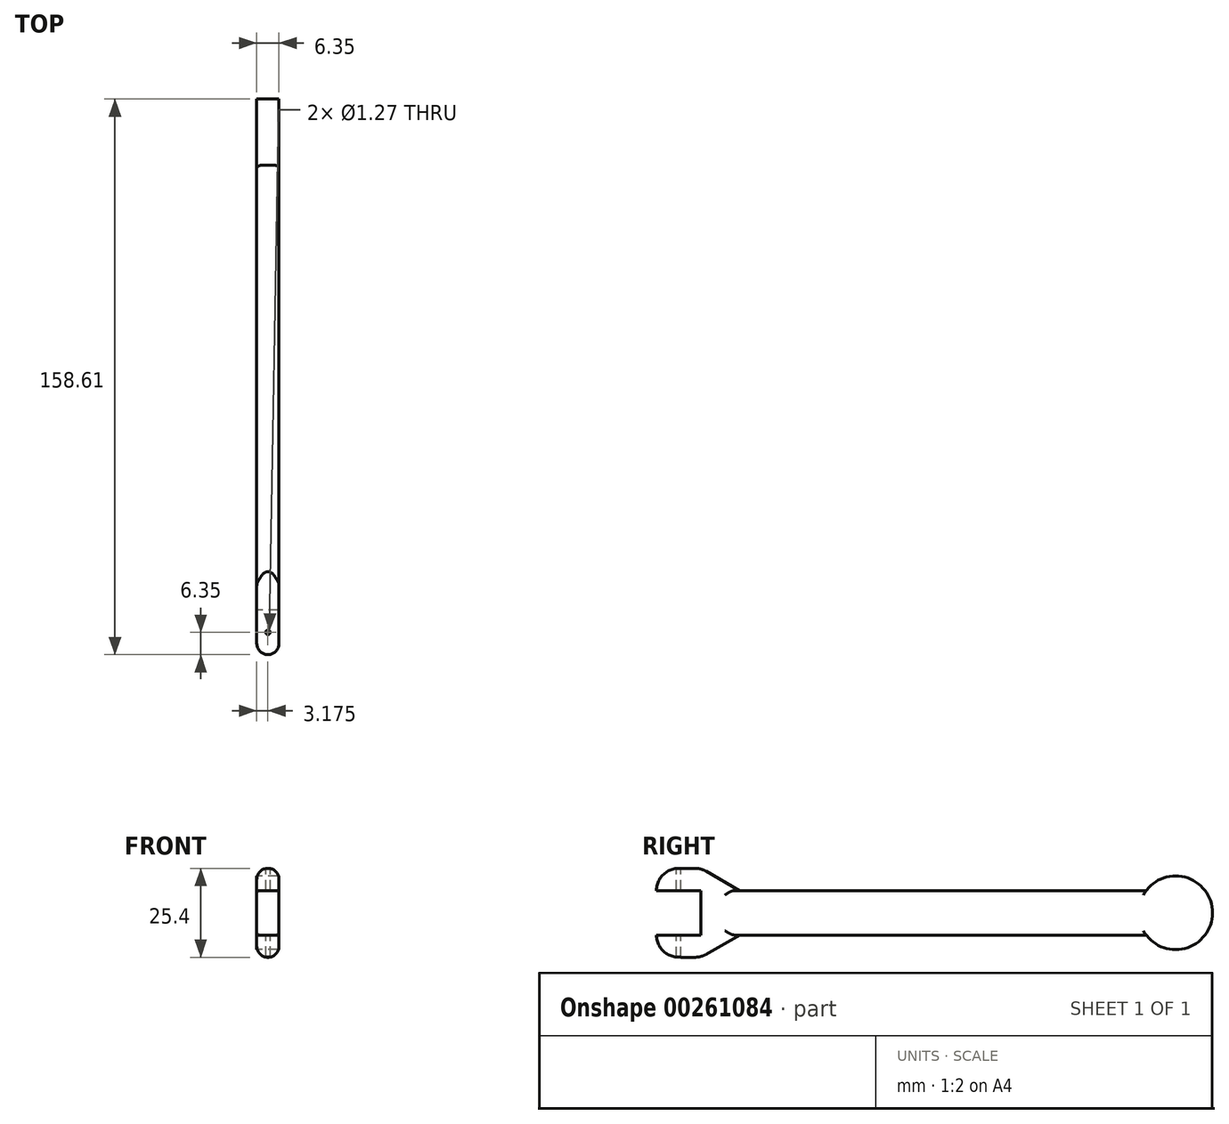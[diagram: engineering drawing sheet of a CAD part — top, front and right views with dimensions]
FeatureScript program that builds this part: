
annotation { "Feature Type Name" : "Feature", "Feature Type Description" : "" }
export const myFeature = defineFeature(function(context is Context, id is Id, definition is map)
    precondition{}
    {
        {
            var Q0;
            Q0=qCreatedBy(makeId("Right.planeOp"),FACE);
            var sketch = newSketch(context, id + "F0", { "sketchPlane" : qUnion([Q0])});
            skLineSegment(sketch, "E0.bottom", {"start": v(63.5, -6.35) * mm, "end": v(-63.5, -6.35) * mm});
            skLineSegment(sketch, "E0.top", {"start": v(63.5, 6.35) * mm, "end": v(-63.5, 6.35) * mm});
            skLineSegment(sketch, "E0.left", {"start": v(63.5, -6.35) * mm, "end": v(63.5, 6.35) * mm});
            skLineSegment(sketch, "E0.right", {"start": v(-63.5, -6.35) * mm, "end": v(-63.5, 6.35) * mm});
            skPoint(sketch, "E0.middle", {"position": v(0, 0) * mm});
            skCircle(sketch, "E1", {"center": v(71.89, 0) * mm, "radius": 10.52 * mm});
            skPoint(sketch, "E1.third.point", {"position": v(82.4, 0) * mm});
            skPoint(sketch, "E1.third.point.positionSnap0", {"position": v(63.5, 0) * mm});
            skLineSegment(sketch, "E2", {"start": v(-63.5, 6.35) * mm, "end": v(-63.5, 12.7) * mm});
            skLineSegment(sketch, "E3.bottom", {"start": v(-63.5, 12.7) * mm, "end": v(-76.2, 12.7) * mm});
            skLineSegment(sketch, "E3.top", {"start": v(-63.5, -12.7) * mm, "end": v(-76.2, -12.7) * mm});
            skLineSegment(sketch, "E3.left", {"start": v(-63.5, 12.7) * mm, "end": v(-63.5, -12.7) * mm});
            skLineSegment(sketch, "E3.right", {"start": v(-76.2, 12.7) * mm, "end": v(-76.2, -12.7) * mm});
            skLineSegment(sketch, "E4.bottom", {"start": v(-63.5, 6.35) * mm, "end": v(-76.2, 6.35) * mm});
            skLineSegment(sketch, "E4.top", {"start": v(-63.5, -6.35) * mm, "end": v(-76.2, -6.35) * mm});
            skLineSegment(sketch, "E4.left", {"start": v(-63.5, 6.35) * mm, "end": v(-63.5, -6.35) * mm});
            skLineSegment(sketch, "E4.right", {"start": v(-76.2, 6.35) * mm, "end": v(-76.2, -6.35) * mm});
            skLineSegment(sketch, "E5", {"start": v(-63.5, 12.7) * mm, "end": v(-52.5, 6.35) * mm});
            skLineSegment(sketch, "E6", {"start": v(-52.5, 6.35) * mm, "end": v(-63.5, 6.35) * mm});
            skLineSegment(sketch, "E7", {"start": v(-63.5, -12.7) * mm, "end": v(-52.5, -6.35) * mm});
            skLineSegment(sketch, "E8", {"start": v(-52.5, -6.35) * mm, "end": v(-63.5, -6.35) * mm});
            skSolve(sketch);
        }
        {
            var Q0;
            {var subQ0=sQuery(id+"F0.wireOp",EDGE,"E0.left");Q0=makeQuery(id+"F0.imprint","IMPRINT",FACE,{"disambiguationData":[TD([[makeQuery(id+"F0.imprint","IMPRINT",EDGE,{"derivedFrom":subQ0}),1.0]])]});}
            var Q1;
            {var subQ0=sQuery(id+"F0.wireOp",EDGE,"E0.left");Q1=makeQuery(id+"F0.imprint","IMPRINT",FACE,{"disambiguationData":[TD([[makeQuery(id+"F0.imprint","IMPRINT",EDGE,{"derivedFrom":subQ0}),-1.0]])]});}
            var Q2;
            {var subQ0=sQuery(id+"F0.wireOp",EDGE,"E0.bottom");Q2=makeQuery(id+"F0.imprint","IMPRINT",FACE,{"disambiguationData":[TD([[makeQuery(id+"F0.imprint","IMPRINT",EDGE,{"derivedFrom":subQ0}),-1.0]])]});}
            var Q3;
            {var subQ0=sQuery(id+"F0.wireOp",EDGE,"E3.bottom");Q3=makeQuery(id+"F0.imprint","IMPRINT",FACE,{"disambiguationData":[TD([[makeQuery(id+"F0.imprint","IMPRINT",EDGE,{"derivedFrom":subQ0}),1.0]])]});}
            var Q4;
            {var subQ0=sQuery(id+"F0.wireOp",EDGE,"E5");Q4=makeQuery(id+"F0.imprint","IMPRINT",FACE,{"disambiguationData":[TD([[makeQuery(id+"F0.imprint","IMPRINT",EDGE,{"derivedFrom":subQ0}),-1.0]])]});}
            var Q5;
            {var subQ0=sQuery(id+"F0.wireOp",EDGE,"E7");Q5=makeQuery(id+"F0.imprint","IMPRINT",FACE,{"disambiguationData":[TD([[makeQuery(id+"F0.imprint","IMPRINT",EDGE,{"derivedFrom":subQ0}),1.0]])]});}
            var Q6;
            {var subQ0=sQuery(id+"F0.wireOp",EDGE,"E3.top");Q6=makeQuery(id+"F0.imprint","IMPRINT",FACE,{"disambiguationData":[TD([[makeQuery(id+"F0.imprint","IMPRINT",EDGE,{"derivedFrom":subQ0}),-1.0]])]});}
            extrude(context, id + "F1", {"entities" : qUnion([Q0, Q1, Q2, Q3, Q4, Q5, Q6]), "depth" : 6.35 * mm});
        }
        {
            var Q0;
            Q0=makeQuery(id+"F1.opExtrude","SWEPT_EDGE",EDGE,{"disambiguationData":[OSD([sQuery(id+"F0.wireOp",EDGE,"E3.bottom"),sQuery(id+"F0.wireOp",EDGE,"E3.right")])]});
            var Q1;
            Q1=makeQuery(id+"F1.opExtrude","SWEPT_EDGE",EDGE,{"disambiguationData":[OSD([sQuery(id+"F0.wireOp",EDGE,"E3.top"),sQuery(id+"F0.wireOp",EDGE,"E3.right")])]});
            fillet(context, id + "F2", {"entities" : qUnion([Q0, Q1]), "radius" : 6.35 * mm, "tangentPropagation" : true, "allowEdgeOverflow" : false});
        }
        {
            var Q0;
            Q0=makeQuery(id+"F1.opExtrude","SWEPT_EDGE",EDGE,{"disambiguationData":[OSD([sQuery(id+"F0.wireOp",EDGE,"E3.bottom"),sQuery(id+"F0.wireOp",EDGE,"E3.left"),sQuery(id+"F0.wireOp",EDGE,"E5")])]});
            var Q1;
            Q1=makeQuery(id+"F1.opExtrude","SWEPT_EDGE",EDGE,{"disambiguationData":[OSD([sQuery(id+"F0.wireOp",EDGE,"E3.top"),sQuery(id+"F0.wireOp",EDGE,"E3.left"),sQuery(id+"F0.wireOp",EDGE,"E7")])]});
            fillet(context, id + "F3", {"entities" : qUnion([Q0, Q1]), "radius" : 6.35 * mm, "tangentPropagation" : true, "allowEdgeOverflow" : false});
        }
        {
            var Q0;
            Q0=makeQuery(id+"F1.opExtrude","SWEPT_FACE",FACE,{"disambiguationData":[OSD([sQuery(id+"F0.wireOp",EDGE,"E3.bottom")])]});
            var sketch = newSketch(context, id + "F4", { "sketchPlane" : qUnion([Q0])});
            skCircle(sketch, "E9", {"center": v(3.18, -69.85) * mm, "radius": 0.64 * mm});
            skSolve(sketch);
        }
        {
            var Q0;
            {var subQ0=sQuery(id+"F4.wireOp",EDGE,"E9");var subQ1=sQuery(id+"F0.wireOp",EDGE,"E3.bottom");var subQ2=makeQuery(id+"F2.opFillet","BLEND_EDGE",EDGE,{"blendedFrom":[makeQuery(id+"F1.opExtrude","SWEPT_EDGE",EDGE,{"disambiguationData":[OSD([subQ1,sQuery(id+"F0.wireOp",EDGE,"E3.right")])]}),makeQuery(id+"F1.opExtrude","SWEPT_FACE",FACE,{"disambiguationData":[OSD([subQ1])]})],"blendedInto":[makeQuery(id+"F1.opExtrude","SWEPT_FACE",FACE,{"disambiguationData":[OSD([subQ1])]})]});var subQ3=makeQuery(id+"F4.imprint","INTERSECT",VERTEX,{"disambiguationData":[OD(0.0)],"derivedFrom":[subQ2,subQ0]});Q0=makeQuery(id+"F4.imprint","IMPRINT",FACE,{"disambiguationData":[TD([[makeQuery(id+"F4.imprint","IMPRINT",EDGE,{"disambiguationData":[TD([[subQ3,1.0]])],"derivedFrom":subQ0}),1.0]])]});}
            var Q1;
            {var subQ0=sQuery(id+"F4.wireOp",EDGE,"E9");var subQ1=sQuery(id+"F0.wireOp",EDGE,"E3.bottom");var subQ2=makeQuery(id+"F2.opFillet","BLEND_EDGE",EDGE,{"blendedFrom":[makeQuery(id+"F1.opExtrude","SWEPT_EDGE",EDGE,{"disambiguationData":[OSD([subQ1,sQuery(id+"F0.wireOp",EDGE,"E3.right")])]}),makeQuery(id+"F1.opExtrude","SWEPT_FACE",FACE,{"disambiguationData":[OSD([subQ1])]})],"blendedInto":[makeQuery(id+"F1.opExtrude","SWEPT_FACE",FACE,{"disambiguationData":[OSD([subQ1])]})]});var subQ3=makeQuery(id+"F4.imprint","INTERSECT",VERTEX,{"disambiguationData":[OD(0.0)],"derivedFrom":[subQ2,subQ0]});Q1=makeQuery(id+"F4.imprint","IMPRINT",FACE,{"disambiguationData":[TD([[makeQuery(id+"F4.imprint","IMPRINT",EDGE,{"disambiguationData":[TD([[subQ3,-1.0]])],"derivedFrom":subQ0}),1.0]])]});}
            extrude(context, id + "F5", {"entities" : qUnion([Q0, Q1]), "operationType" : NewBodyOperationType.REMOVE, "oppositeDirection" : true, "depth" : 25.4 * mm});
        }
        {
            var Q0;
            Q0=makeQuery(id+"F1.opExtrude","CAP_EDGE",EDGE,{"disambiguationData":[OSD([sQuery(id+"F0.wireOp",EDGE,"E0.bottom")])],"isStart":false});
            var Q1;
            Q1=makeQuery(id+"F1.opExtrude","CAP_EDGE",EDGE,{"disambiguationData":[OSD([sQuery(id+"F0.wireOp",EDGE,"E0.bottom")])],"isStart":true});
            var Q2;
            Q2=makeQuery(id+"F1.opExtrude","CAP_EDGE",EDGE,{"disambiguationData":[OSD([sQuery(id+"F0.wireOp",EDGE,"E0.top")])],"isStart":false});
            var Q3;
            Q3=makeQuery(id+"F1.opExtrude","CAP_EDGE",EDGE,{"disambiguationData":[OSD([sQuery(id+"F0.wireOp",EDGE,"E0.top")])],"isStart":true});
            fillet(context, id + "F6", {"entities" : qUnion([Q0, Q1, Q2, Q3]), "radius" : 1.27 * mm, "tangentPropagation" : true, "allowEdgeOverflow" : false});
        }
        {
            var Q0;
            {var subQ0=sQuery(id+"F0.wireOp",EDGE,"E3.right");var subQ1=sQuery(id+"F0.wireOp",EDGE,"E3.bottom");Q0=makeQuery(id+"F2.opFillet","BLEND_EDGE",EDGE,{"blendedFrom":[makeQuery(id+"F1.opExtrude","SWEPT_EDGE",EDGE,{"disambiguationData":[OSD([subQ1,subQ0])]}),makeQuery(id+"F1.opExtrude","CAP_FACE",FACE,{"disambiguationData":[OSD([sQuery(id+"F0.wireOp",EDGE,"E0.bottom"),sQuery(id+"F0.wireOp",EDGE,"E0.top"),sQuery(id+"F0.wireOp",EDGE,"E1"),subQ1,sQuery(id+"F0.wireOp",EDGE,"E3.top"),subQ0,sQuery(id+"F0.wireOp",EDGE,"E4.bottom"),sQuery(id+"F0.wireOp",EDGE,"E4.top"),sQuery(id+"F0.wireOp",EDGE,"E4.left"),sQuery(id+"F0.wireOp",EDGE,"E5"),sQuery(id+"F0.wireOp",EDGE,"E7")])],"isStart":true})],"blendedInto":[makeQuery(id+"F1.opExtrude","CAP_FACE",FACE,{"disambiguationData":[OSD([sQuery(id+"F0.wireOp",EDGE,"E0.bottom"),sQuery(id+"F0.wireOp",EDGE,"E0.top"),sQuery(id+"F0.wireOp",EDGE,"E1"),subQ1,sQuery(id+"F0.wireOp",EDGE,"E3.top"),subQ0,sQuery(id+"F0.wireOp",EDGE,"E4.bottom"),sQuery(id+"F0.wireOp",EDGE,"E4.top"),sQuery(id+"F0.wireOp",EDGE,"E4.left"),sQuery(id+"F0.wireOp",EDGE,"E5"),sQuery(id+"F0.wireOp",EDGE,"E7")])],"isStart":true})]});}
            var Q1;
            {var subQ0=sQuery(id+"F0.wireOp",EDGE,"E3.right");var subQ1=sQuery(id+"F0.wireOp",EDGE,"E3.bottom");Q1=makeQuery(id+"F2.opFillet","BLEND_EDGE",EDGE,{"blendedFrom":[makeQuery(id+"F1.opExtrude","SWEPT_EDGE",EDGE,{"disambiguationData":[OSD([subQ1,subQ0])]}),makeQuery(id+"F1.opExtrude","CAP_FACE",FACE,{"disambiguationData":[OSD([sQuery(id+"F0.wireOp",EDGE,"E0.bottom"),sQuery(id+"F0.wireOp",EDGE,"E0.top"),sQuery(id+"F0.wireOp",EDGE,"E1"),subQ1,sQuery(id+"F0.wireOp",EDGE,"E3.top"),subQ0,sQuery(id+"F0.wireOp",EDGE,"E4.bottom"),sQuery(id+"F0.wireOp",EDGE,"E4.top"),sQuery(id+"F0.wireOp",EDGE,"E4.left"),sQuery(id+"F0.wireOp",EDGE,"E5"),sQuery(id+"F0.wireOp",EDGE,"E7")])],"isStart":false})],"blendedInto":[makeQuery(id+"F1.opExtrude","CAP_FACE",FACE,{"disambiguationData":[OSD([sQuery(id+"F0.wireOp",EDGE,"E0.bottom"),sQuery(id+"F0.wireOp",EDGE,"E0.top"),sQuery(id+"F0.wireOp",EDGE,"E1"),subQ1,sQuery(id+"F0.wireOp",EDGE,"E3.top"),subQ0,sQuery(id+"F0.wireOp",EDGE,"E4.bottom"),sQuery(id+"F0.wireOp",EDGE,"E4.top"),sQuery(id+"F0.wireOp",EDGE,"E4.left"),sQuery(id+"F0.wireOp",EDGE,"E5"),sQuery(id+"F0.wireOp",EDGE,"E7")])],"isStart":false})]});}
            var Q2;
            {var subQ0=sQuery(id+"F0.wireOp",EDGE,"E3.right");var subQ1=sQuery(id+"F0.wireOp",EDGE,"E3.top");Q2=makeQuery(id+"F2.opFillet","BLEND_EDGE",EDGE,{"blendedFrom":[makeQuery(id+"F1.opExtrude","SWEPT_EDGE",EDGE,{"disambiguationData":[OSD([subQ1,subQ0])]}),makeQuery(id+"F1.opExtrude","CAP_FACE",FACE,{"disambiguationData":[OSD([sQuery(id+"F0.wireOp",EDGE,"E0.bottom"),sQuery(id+"F0.wireOp",EDGE,"E0.top"),sQuery(id+"F0.wireOp",EDGE,"E1"),sQuery(id+"F0.wireOp",EDGE,"E3.bottom"),subQ1,subQ0,sQuery(id+"F0.wireOp",EDGE,"E4.bottom"),sQuery(id+"F0.wireOp",EDGE,"E4.top"),sQuery(id+"F0.wireOp",EDGE,"E4.left"),sQuery(id+"F0.wireOp",EDGE,"E5"),sQuery(id+"F0.wireOp",EDGE,"E7")])],"isStart":true})],"blendedInto":[makeQuery(id+"F1.opExtrude","CAP_FACE",FACE,{"disambiguationData":[OSD([sQuery(id+"F0.wireOp",EDGE,"E0.bottom"),sQuery(id+"F0.wireOp",EDGE,"E0.top"),sQuery(id+"F0.wireOp",EDGE,"E1"),sQuery(id+"F0.wireOp",EDGE,"E3.bottom"),subQ1,subQ0,sQuery(id+"F0.wireOp",EDGE,"E4.bottom"),sQuery(id+"F0.wireOp",EDGE,"E4.top"),sQuery(id+"F0.wireOp",EDGE,"E4.left"),sQuery(id+"F0.wireOp",EDGE,"E5"),sQuery(id+"F0.wireOp",EDGE,"E7")])],"isStart":true})]});}
            var Q3;
            {var subQ0=sQuery(id+"F0.wireOp",EDGE,"E3.right");var subQ1=sQuery(id+"F0.wireOp",EDGE,"E3.top");Q3=makeQuery(id+"F2.opFillet","BLEND_EDGE",EDGE,{"blendedFrom":[makeQuery(id+"F1.opExtrude","SWEPT_EDGE",EDGE,{"disambiguationData":[OSD([subQ1,subQ0])]}),makeQuery(id+"F1.opExtrude","CAP_FACE",FACE,{"disambiguationData":[OSD([sQuery(id+"F0.wireOp",EDGE,"E0.bottom"),sQuery(id+"F0.wireOp",EDGE,"E0.top"),sQuery(id+"F0.wireOp",EDGE,"E1"),sQuery(id+"F0.wireOp",EDGE,"E3.bottom"),subQ1,subQ0,sQuery(id+"F0.wireOp",EDGE,"E4.bottom"),sQuery(id+"F0.wireOp",EDGE,"E4.top"),sQuery(id+"F0.wireOp",EDGE,"E4.left"),sQuery(id+"F0.wireOp",EDGE,"E5"),sQuery(id+"F0.wireOp",EDGE,"E7")])],"isStart":false})],"blendedInto":[makeQuery(id+"F1.opExtrude","CAP_FACE",FACE,{"disambiguationData":[OSD([sQuery(id+"F0.wireOp",EDGE,"E0.bottom"),sQuery(id+"F0.wireOp",EDGE,"E0.top"),sQuery(id+"F0.wireOp",EDGE,"E1"),sQuery(id+"F0.wireOp",EDGE,"E3.bottom"),subQ1,subQ0,sQuery(id+"F0.wireOp",EDGE,"E4.bottom"),sQuery(id+"F0.wireOp",EDGE,"E4.top"),sQuery(id+"F0.wireOp",EDGE,"E4.left"),sQuery(id+"F0.wireOp",EDGE,"E5"),sQuery(id+"F0.wireOp",EDGE,"E7")])],"isStart":false})]});}
            fillet(context, id + "F7", {"entities" : qUnion([Q0, Q1, Q2, Q3]), "radius" : 3.17 * mm, "tangentPropagation" : true, "allowEdgeOverflow" : false});
        }
    });
